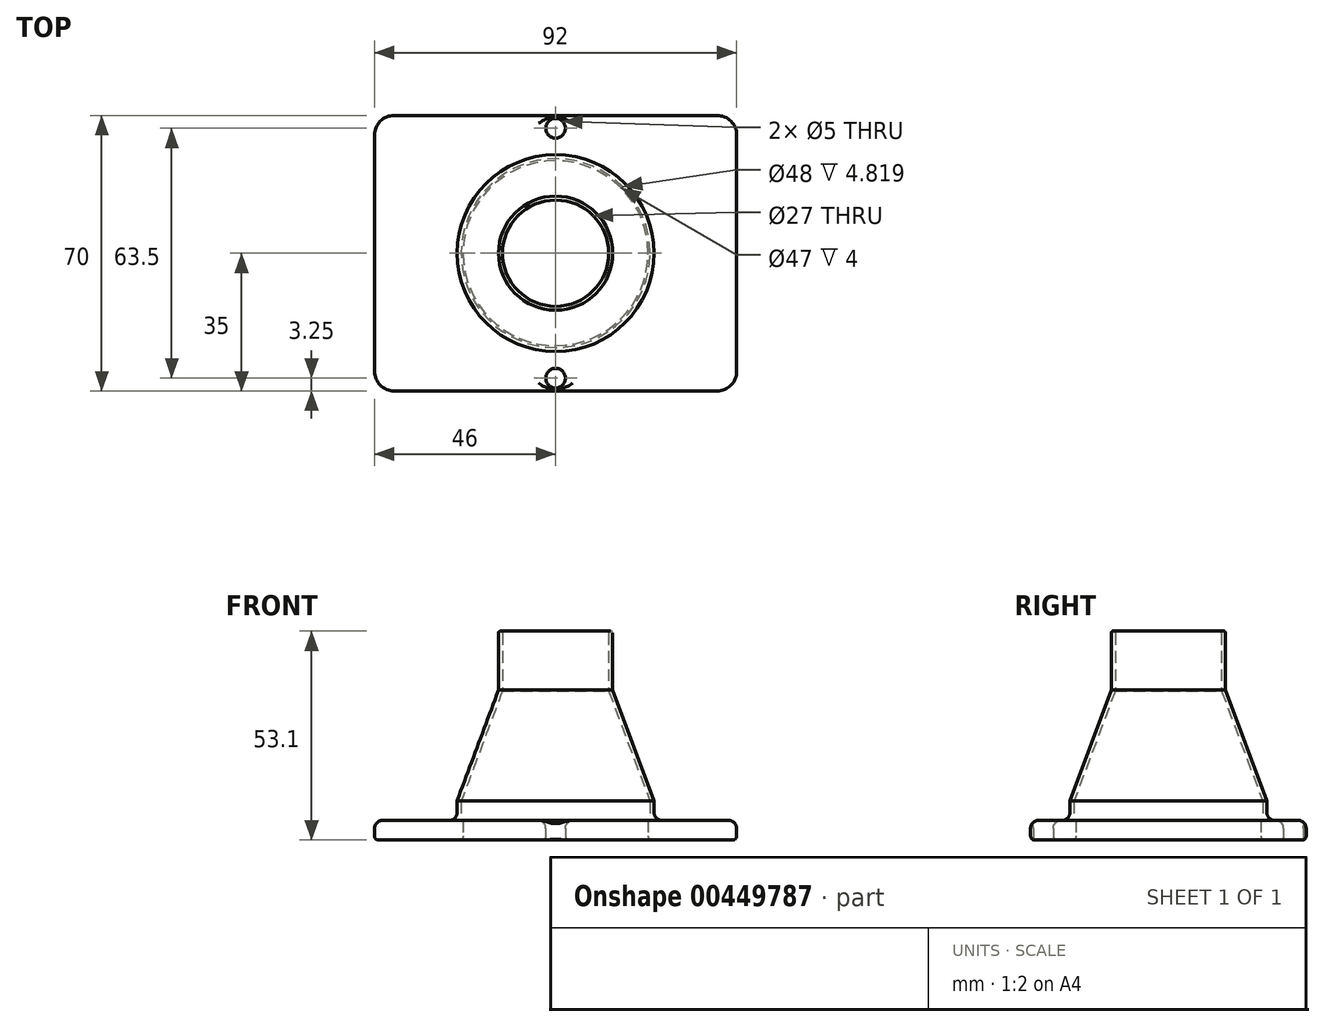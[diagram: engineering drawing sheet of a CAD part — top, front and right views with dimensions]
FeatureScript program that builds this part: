
annotation { "Feature Type Name" : "Feature", "Feature Type Description" : "" }
export const myFeature = defineFeature(function(context is Context, id is Id, definition is map)
    precondition{}
    {
        {
            var Q0;
            Q0=qCreatedBy(makeId("Front.planeOp"),FACE);
            var sketch = newSketch(context, id + "F0", { "sketchPlane" : qUnion([Q0])});
            skLineSegment(sketch, "E0", {"start": v(-25, 0) * mm, "end": v(-25, 10) * mm});
            skLineSegment(sketch, "E1", {"start": v(-25, 10) * mm, "end": v(-14.5, 38.1) * mm});
            skLineSegment(sketch, "E2", {"start": v(-14.5, 38.1) * mm, "end": v(-14.5, 53.1) * mm});
            skLineSegment(sketch, "E3.0", {"start": v(-13.5, 37.92) * mm, "end": v(-13.5, 53.1) * mm});
            skLineSegment(sketch, "E3.1", {"start": v(-24, 9.82) * mm, "end": v(-13.5, 37.92) * mm});
            skLineSegment(sketch, "E3.2", {"start": v(-24, 0) * mm, "end": v(-24, 9.82) * mm});
            skLineSegment(sketch, "E4", {"start": v(-25, 0) * mm, "end": v(-24, 0) * mm});
            skLineSegment(sketch, "E5", {"start": v(-14.5, 53.1) * mm, "end": v(-13.5, 53.1) * mm});
            skLineSegment(sketch, "E6", {"start": v(0, 0) * mm, "end": v(0, 46.9) * mm, "construction": true});
            skSolve(sketch);
        }
        {
            var Q0;
            Q0=makeQuery(id+"F0.imprint","IMPRINT",FACE,{"disambiguationData":[TD([[makeQuery(id+"F0.imprint","IMPRINT",EDGE,{"derivedFrom":sQuery(id+"F0.wireOp",EDGE,"E0")}),-1.0]])]});
            var Q1;
            Q1=sQuery(id+"F0.wireOp",EDGE,"E6");
            revolve(context, id + "F1", {"entities" : qUnion([Q0]), "axis" : qUnion([Q1]), "revolveType" : RevolveType.FULL});
        }
        {
            var Q0;
            Q0=makeQuery(id+"F1.opRevolve","SWEPT_FACE",FACE,{"disambiguationData":[OSD([sQuery(id+"F0.wireOp",EDGE,"E4")])]});
            cPlane(context, id + "F2", {"entities" : qUnion([Q0]), "cplaneType" : CPlaneType.OFFSET, "offset" : 0 * mm, "width" : 150 * mm, "height" : 150 * mm});
        }
        {
            var Q0;
            Q0=qCreatedBy(id+"F2.planeOp",FACE);
            var sketch = newSketch(context, id + "F3", { "sketchPlane" : qUnion([Q0])});
            skLineSegment(sketch, "E7.bottom", {"start": v(-46, 35) * mm, "end": v(46, 35) * mm});
            skLineSegment(sketch, "E7.top", {"start": v(-46, -35) * mm, "end": v(46, -35) * mm});
            skLineSegment(sketch, "E7.left", {"start": v(-46, 35) * mm, "end": v(-46, -35) * mm});
            skLineSegment(sketch, "E7.right", {"start": v(46, 35) * mm, "end": v(46, -35) * mm});
            skPoint(sketch, "E7.middle", {"position": v(0, 0) * mm});
            skLineSegment(sketch, "E8", {"start": v(0, 37.22) * mm, "end": v(0, -35) * mm, "construction": true});
            skCircle(sketch, "E9", {"center": v(0, 31.75) * mm, "radius": 2.5 * mm});
            skLineSegment(sketch, "E10", {"start": v(-42.64, 0) * mm, "end": v(31.16, 0) * mm, "construction": true});
            skCircle(sketch, "E11.MirrorC", {"center": v(0, -31.75) * mm, "radius": 2.5 * mm});
            skSolve(sketch);
        }
        {
            var Q0;
            Q0=makeQuery(id+"F3.imprint","IMPRINT",FACE,{"disambiguationData":[TD([[makeQuery(id+"F3.imprint","IMPRINT",EDGE,{"derivedFrom":sQuery(id+"F3.wireOp",EDGE,"E7.bottom")}),-1.0]])]});
            extrude(context, id + "F4", {"entities" : qUnion([Q0]), "operationType" : NewBodyOperationType.ADD, "oppositeDirection" : true, "depth" : 5 * mm});
        }
        {
            var Q0;
            Q0=makeQuery(id+"F4.boolean.opBoolean","MERGE",FACE,{"derivedFrom":[makeQuery(id+"F1.opRevolve","SWEPT_FACE",FACE,{"disambiguationData":[OSD([sQuery(id+"F0.wireOp",EDGE,"E4")])]}),makeQuery(id+"F4.opExtrude","CAP_FACE",FACE,{"disambiguationData":[OSD([sQuery(id+"F3.wireOp",EDGE,"E7.bottom"),sQuery(id+"F3.wireOp",EDGE,"E7.top"),sQuery(id+"F3.wireOp",EDGE,"E7.left"),sQuery(id+"F3.wireOp",EDGE,"E7.right"),sQuery(id+"F3.wireOp",EDGE,"E9"),sQuery(id+"F3.wireOp",EDGE,"E11.MirrorC")])],"isStart":true})]});
            var sketch = newSketch(context, id + "F5", { "sketchPlane" : qUnion([Q0])});
            skCircle(sketch, "E12", {"center": v(0, 0) * mm, "radius": 23.5 * mm});
            skSolve(sketch);
        }
        {
            var Q0;
            Q0 = qSketchRegion(id + "F5", true);
            extrude(context, id + "F6", {"entities" : qUnion([Q0]), "operationType" : NewBodyOperationType.REMOVE, "endBound" : BoundingType.UP_TO_NEXT, "oppositeDirection" : true, "depth" : 25 * mm});
        }
        {
            var Q0;
            {var subQ0=sQuery(id+"F3.wireOp",EDGE,"E7.left");var subQ1=sQuery(id+"F3.wireOp",EDGE,"E7.top");var subQ2=sQuery(id+"F3.wireOp",EDGE,"E7.bottom");var subQ3=sQuery(id+"F3.wireOp",EDGE,"E9");var subQ4=sQuery(id+"F3.wireOp",EDGE,"E7.right");var subQ5=sQuery(id+"F3.wireOp",EDGE,"E11.MirrorC");Q0=makeQuery(id+"F4.boolean.opBoolean","SPLIT",FACE,{"disambiguationData":[TD([makeQuery(id+"F1.opRevolve","SWEPT_FACE",FACE,{"disambiguationData":[OSD([sQuery(id+"F0.wireOp",EDGE,"E0")])]})])],"derivedFrom":makeQuery(id+"F4.opExtrude","CAP_FACE",FACE,{"disambiguationData":[OSD([subQ2,subQ1,subQ0,subQ4,subQ3,subQ5])],"isStart":false})});}
            fillet(context, id + "F7", {"entities" : qUnion([Q0]), "radius" : 2 * mm, "tangentPropagation" : true, "allowEdgeOverflow" : false});
        }
        {
            var Q0;
            Q0=makeQuery(id+"F4.opExtrude","SWEPT_EDGE",EDGE,{"disambiguationData":[OSD([sQuery(id+"F3.wireOp",EDGE,"E7.bottom"),sQuery(id+"F3.wireOp",EDGE,"E7.right")])]});
            var Q1;
            Q1=makeQuery(id+"F4.opExtrude","SWEPT_EDGE",EDGE,{"disambiguationData":[OSD([sQuery(id+"F3.wireOp",EDGE,"E7.bottom"),sQuery(id+"F3.wireOp",EDGE,"E7.left")])]});
            var Q2;
            Q2=makeQuery(id+"F4.opExtrude","SWEPT_EDGE",EDGE,{"disambiguationData":[OSD([sQuery(id+"F3.wireOp",EDGE,"E7.top"),sQuery(id+"F3.wireOp",EDGE,"E7.left")])]});
            var Q3;
            Q3=makeQuery(id+"F4.opExtrude","SWEPT_EDGE",EDGE,{"disambiguationData":[OSD([sQuery(id+"F3.wireOp",EDGE,"E7.top"),sQuery(id+"F3.wireOp",EDGE,"E7.right")])]});
            fillet(context, id + "F8", {"entities" : qUnion([Q0, Q1, Q2, Q3]), "radius" : 5 * mm, "tangentPropagation" : true, "allowEdgeOverflow" : false});
        }
        {
            var Q0;
            Q0=makeQuery(id+"F1.opRevolve","SWEPT_FACE",FACE,{"disambiguationData":[OSD([sQuery(id+"F0.wireOp",EDGE,"E5")])]});
            fillet(context, id + "F9", {"entities" : qUnion([Q0]), "radius" : .5 * mm, "tangentPropagation" : true, "allowEdgeOverflow" : false});
        }
        {
            var Q0;
            Q0=makeQuery(id+"F4.boolean.opBoolean","MERGE",FACE,{"derivedFrom":[makeQuery(id+"F1.opRevolve","SWEPT_FACE",FACE,{"disambiguationData":[OSD([sQuery(id+"F0.wireOp",EDGE,"E4")])]}),makeQuery(id+"F4.opExtrude","CAP_FACE",FACE,{"disambiguationData":[OSD([sQuery(id+"F3.wireOp",EDGE,"E7.bottom"),sQuery(id+"F3.wireOp",EDGE,"E7.top"),sQuery(id+"F3.wireOp",EDGE,"E7.left"),sQuery(id+"F3.wireOp",EDGE,"E7.right"),sQuery(id+"F3.wireOp",EDGE,"E9"),sQuery(id+"F3.wireOp",EDGE,"E11.MirrorC")])],"isStart":true})]});
            fillet(context, id + "F10", {"entities" : qUnion([Q0]), "radius" : 1 * mm, "tangentPropagation" : true, "allowEdgeOverflow" : false});
        }
    });
